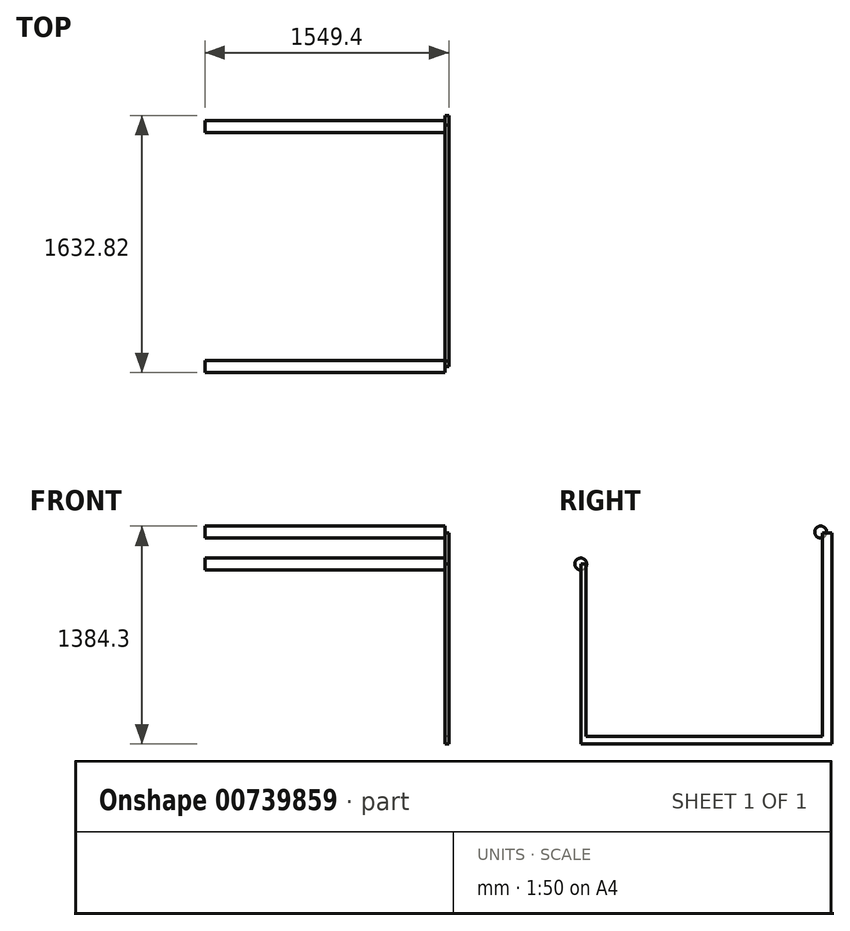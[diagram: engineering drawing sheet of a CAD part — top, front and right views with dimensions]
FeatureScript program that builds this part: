
annotation { "Feature Type Name" : "Feature", "Feature Type Description" : "" }
export const myFeature = defineFeature(function(context is Context, id is Id, definition is map)
    precondition{}
    {
        {
            var Q0;
            Q0=qCreatedBy(makeId("Right.planeOp"),FACE);
            var sketch = newSketch(context, id + "F0", { "sketchPlane" : qUnion([Q0])});
            skLineSegment(sketch, "E0", {"start": v(0, 0) * mm, "end": v(0, 1143) * mm});
            skLineSegment(sketch, "E1", {"start": v(0, 0) * mm, "end": v(1524, 0) * mm});
            skLineSegment(sketch, "E2", {"start": v(1524, 0) * mm, "end": v(1524, 1346.2) * mm});
            skCircle(sketch, "E3", {"center": v(0, 1143) * mm, "radius": 38.1 * mm});
            skCircle(sketch, "E4", {"center": v(1524, 1346.2) * mm, "radius": 38.1 * mm});
            skSolve(sketch);
        }
        {
            var Q0;
            Q0=makeQuery(id+"F0.imprint","IMPRINT",FACE,{"disambiguationData":[TD([[makeQuery(id+"F0.imprint","IMPRINT",EDGE,{"derivedFrom":sQuery(id+"F0.wireOp",EDGE,"E3")}),1.0]])]});
            var Q1;
            Q1=makeQuery(id+"F0.imprint","IMPRINT",FACE,{"disambiguationData":[TD([[makeQuery(id+"F0.imprint","IMPRINT",EDGE,{"derivedFrom":sQuery(id+"F0.wireOp",EDGE,"E4")}),1.0]])]});
            extrude(context, id + "F1", {"entities" : qUnion([Q0, Q1]), "oppositeDirection" : true, "depth" : 1524 * mm, "offsetDistance" : 25.4 * mm});
        }
        {
            var Q0;
            Q0=qCreatedBy(makeId("Right.planeOp"),FACE);
            var sketch = newSketch(context, id + "F2", { "sketchPlane" : qUnion([Q0])});
            skLineSegment(sketch, "E5.bottom", {"start": v(0, 1142.78) * mm, "end": v(34.13, 1142.78) * mm});
            skLineSegment(sketch, "E5.top", {"start": v(0, 0) * mm, "end": v(34.13, 0) * mm});
            skLineSegment(sketch, "E5.left", {"start": v(0, 1142.78) * mm, "end": v(0, 0) * mm});
            skLineSegment(sketch, "E5.right", {"start": v(34.13, 1142.78) * mm, "end": v(34.13, 0) * mm});
            skLineSegment(sketch, "E6.bottom", {"start": v(1534.6, 1341.61) * mm, "end": v(1594.72, 1341.61) * mm});
            skLineSegment(sketch, "E6.top", {"start": v(1534.6, 0) * mm, "end": v(1594.72, 0) * mm});
            skLineSegment(sketch, "E6.left", {"start": v(1534.6, 1341.61) * mm, "end": v(1534.6, 0) * mm});
            skLineSegment(sketch, "E6.right", {"start": v(1594.72, 1341.61) * mm, "end": v(1594.72, 0) * mm});
            skLineSegment(sketch, "E7.bottom", {"start": v(0, 47.58) * mm, "end": v(1534.6, 47.58) * mm});
            skLineSegment(sketch, "E7.top", {"start": v(0, 0) * mm, "end": v(1534.6, 0) * mm});
            skLineSegment(sketch, "E7.left", {"start": v(0, 47.58) * mm, "end": v(0, 0) * mm});
            skLineSegment(sketch, "E7.right", {"start": v(1534.6, 47.58) * mm, "end": v(1534.6, 0) * mm});
            skSolve(sketch);
        }
        {
            var Q0;
            {var subQ0=sQuery(id+"F2.wireOp",EDGE,"E5.top");Q0=makeQuery(id+"F2.imprint","IMPRINT",FACE,{"disambiguationData":[TD([[makeQuery(id+"F2.imprint","IMPRINT",EDGE,{"derivedFrom":subQ0}),1.0]])]});}
            var Q1;
            {var subQ3=sQuery(id+"F2.wireOp",EDGE,"E6.bottom");Q1=makeQuery(id+"F2.imprint","IMPRINT",FACE,{"disambiguationData":[TD([[makeQuery(id+"F2.imprint","IMPRINT",EDGE,{"derivedFrom":subQ3}),-1.0]])]});}
            var Q2;
            {var subQ0=sQuery(id+"F2.wireOp",EDGE,"E7.top");Q2=makeQuery(id+"F2.imprint","IMPRINT",FACE,{"disambiguationData":[TD([[makeQuery(id+"F2.imprint","IMPRINT",EDGE,{"derivedFrom":subQ0}),1.0]])]});}
            var Q3;
            {var subQ0=sQuery(id+"F2.wireOp",EDGE,"E5.bottom");Q3=makeQuery(id+"F2.imprint","IMPRINT",FACE,{"disambiguationData":[TD([[makeQuery(id+"F2.imprint","IMPRINT",EDGE,{"derivedFrom":subQ0}),-1.0]])]});}
            extrude(context, id + "F3", {"entities" : qUnion([Q0, Q1, Q2, Q3]), "depth" : 25.4 * mm, "offsetDistance" : 25.4 * mm});
        }
    });
